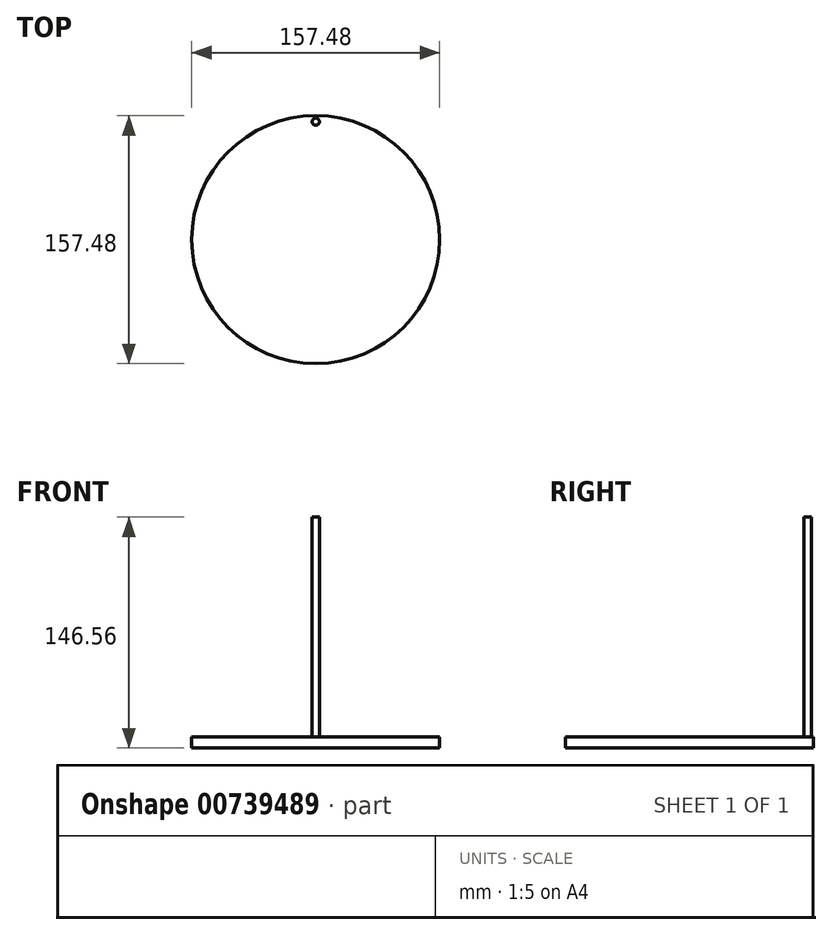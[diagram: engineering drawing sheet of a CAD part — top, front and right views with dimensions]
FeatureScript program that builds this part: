
annotation { "Feature Type Name" : "Feature", "Feature Type Description" : "" }
export const myFeature = defineFeature(function(context is Context, id is Id, definition is map)
    precondition{}
    {
        {
            var Q0;
            Q0=qCreatedBy(makeId("Top.planeOp"),FACE);
            var sketch = newSketch(context, id + "F0", { "sketchPlane" : qUnion([Q0])});
            skCircle(sketch, "E0", {"center": v(0, 0) * mm, "radius": 78.74 * mm});
            skSolve(sketch);
        }
        {
            var Q0;
            Q0 = qSketchRegion(id + "F0", true);
            extrude(context, id + "F1", {"entities" : qUnion([Q0]), "oppositeDirection" : true, "depth" : 74.17 * mm, "offsetDistance" : 25.4 * mm, "hasSecondDirection" : true, "secondDirectionOppositeDirection" : true, "secondDirectionDepth" : 67.3 * mm});
        }
        {
            var Q0;
            Q0=makeQuery(id+"F1.opExtrude","CAP_FACE",FACE,{"disambiguationData":[OSD([sQuery(id+"F0.wireOp",EDGE,"E0")])],"isStart":true});
            var sketch = newSketch(context, id + "F2", { "sketchPlane" : qUnion([Q0])});
            skPoint(sketch, "E1", {"position": v(0, 0) * mm});
            skCircle(sketch, "E2", {"center": v(0, 74.89) * mm, "radius": 2.29 * mm});
            skSolve(sketch);
        }
        {
            var Q0;
            Q0 = qSketchRegion(id + "F2", true);
            extrude(context, id + "F3", {"entities" : qUnion([Q0]), "operationType" : NewBodyOperationType.ADD, "depth" : 139.7 * mm, "offsetDistance" : 25.4 * mm});
        }
        {
            var Q0;
            Q0=qCreatedBy(makeId("Right.planeOp"),FACE);
            var sketch = newSketch(context, id + "F4", { "sketchPlane" : qUnion([Q0])});
            skLineSegment(sketch, "E3", {"start": v(0, 5.68) * mm, "end": v(0, -75.4) * mm});
            skSolve(sketch);
        }
    });
